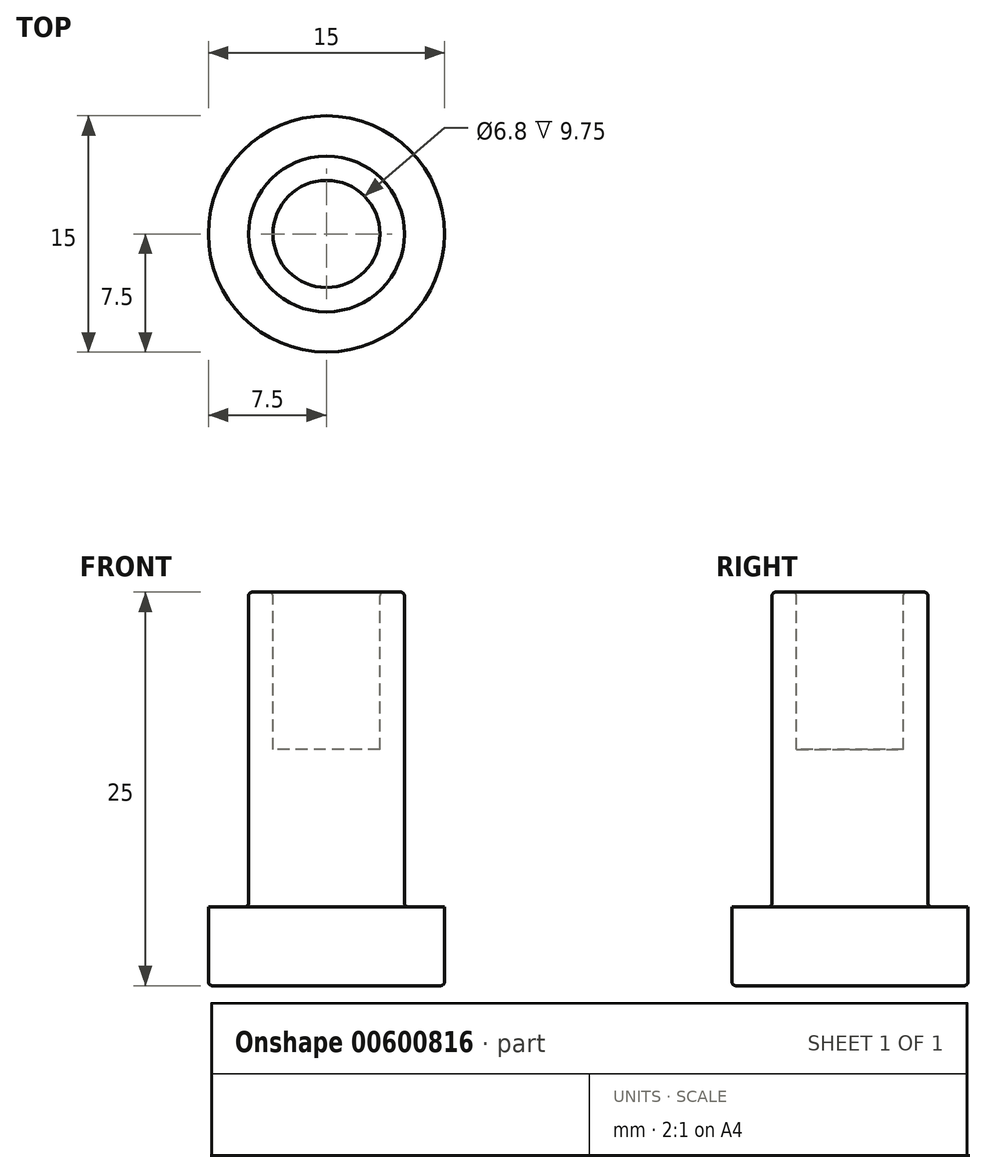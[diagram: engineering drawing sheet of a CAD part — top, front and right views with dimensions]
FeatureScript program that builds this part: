
annotation { "Feature Type Name" : "Feature", "Feature Type Description" : "" }
export const myFeature = defineFeature(function(context is Context, id is Id, definition is map)
    precondition{}
    {
        {
            var Q0;
            Q0=qCreatedBy(makeId("Top.planeOp"),FACE);
            var sketch = newSketch(context, id + "F0", { "sketchPlane" : qUnion([Q0])});
            skCircle(sketch, "E0", {"center": v(0, 0) * mm, "radius": 7.5 * mm});
            skSolve(sketch);
        }
        {
            var Q0;
            Q0 = qSketchRegion(id + "F0", true);
            extrude(context, id + "F1", {"entities" : qUnion([Q0]), "depth" : 25 * mm, "offsetDistance" : 25 * mm});
        }
        {
            var Q0;
            Q0=makeQuery(id+"F1.opExtrude","CAP_FACE",FACE,{"disambiguationData":[OSD([sQuery(id+"F0.wireOp",EDGE,"E0")])],"isStart":false});
            var sketch = newSketch(context, id + "F2", { "sketchPlane" : qUnion([Q0])});
            skCircle(sketch, "E1", {"center": v(0, 0) * mm, "radius": 4.95 * mm});
            skSolve(sketch);
        }
        {
            var Q0;
            Q0=makeQuery(id+"F2.imprint","IMPRINT",FACE,{"disambiguationData":[TD([[makeQuery(id+"F2.imprint","IMPRINT",EDGE,{"derivedFrom":sQuery(id+"F2.wireOp",EDGE,"E1")}),-1.0]])]});
            extrude(context, id + "F3", {"entities" : qUnion([Q0]), "operationType" : NewBodyOperationType.REMOVE, "oppositeDirection" : true, "depth" : 20 * mm, "offsetDistance" : 25 * mm});
        }
        {
            var Q0;
            Q0=makeQuery(id+"F1.opExtrude","CAP_FACE",FACE,{"disambiguationData":[OSD([sQuery(id+"F0.wireOp",EDGE,"E0")])],"isStart":false});
            var sketch = newSketch(context, id + "F4", { "sketchPlane" : qUnion([Q0])});
            skCircle(sketch, "E2", {"center": v(0, 0) * mm, "radius": 3.4 * mm});
            skSolve(sketch);
        }
        {
            var Q0;
            Q0 = qSketchRegion(id + "F4", true);
            extrude(context, id + "F5", {"entities" : qUnion([Q0]), "operationType" : NewBodyOperationType.REMOVE, "oppositeDirection" : true, "depth" : 10 * mm, "offsetDistance" : 25 * mm});
        }
        {
            var Q0;
            Q0=makeQuery(id+"F3.boolean.opBoolean","COPY",EDGE,{"derivedFrom":makeQuery(id+"F3.opExtrude","CAP_EDGE",EDGE,{"disambiguationData":[OSD([sQuery(id+"F0.wireOp",EDGE,"E0")])],"isStart":false})});
            var Q1;
            Q1=makeQuery(id+"F1.opExtrude","CAP_FACE",FACE,{"disambiguationData":[OSD([sQuery(id+"F0.wireOp",EDGE,"E0")])],"isStart":true});
            var Q2;
            Q2=makeQuery(id+"F1.opExtrude","CAP_FACE",FACE,{"disambiguationData":[OSD([sQuery(id+"F0.wireOp",EDGE,"E0")])],"isStart":false});
            var Q3;
            Q3=makeQuery(id+"F3.boolean.opBoolean","COPY",EDGE,{"derivedFrom":makeQuery(id+"F3.opExtrude","CAP_EDGE",EDGE,{"disambiguationData":[OSD([sQuery(id+"F2.wireOp",EDGE,"E1")])],"isStart":false})});
            fillet(context, id + "F6", {"entities" : qUnion([Q0, Q1, Q2, Q3]), "radius" : 0.25 * mm, "tangentPropagation" : true, "allowEdgeOverflow" : false});
        }
    });
